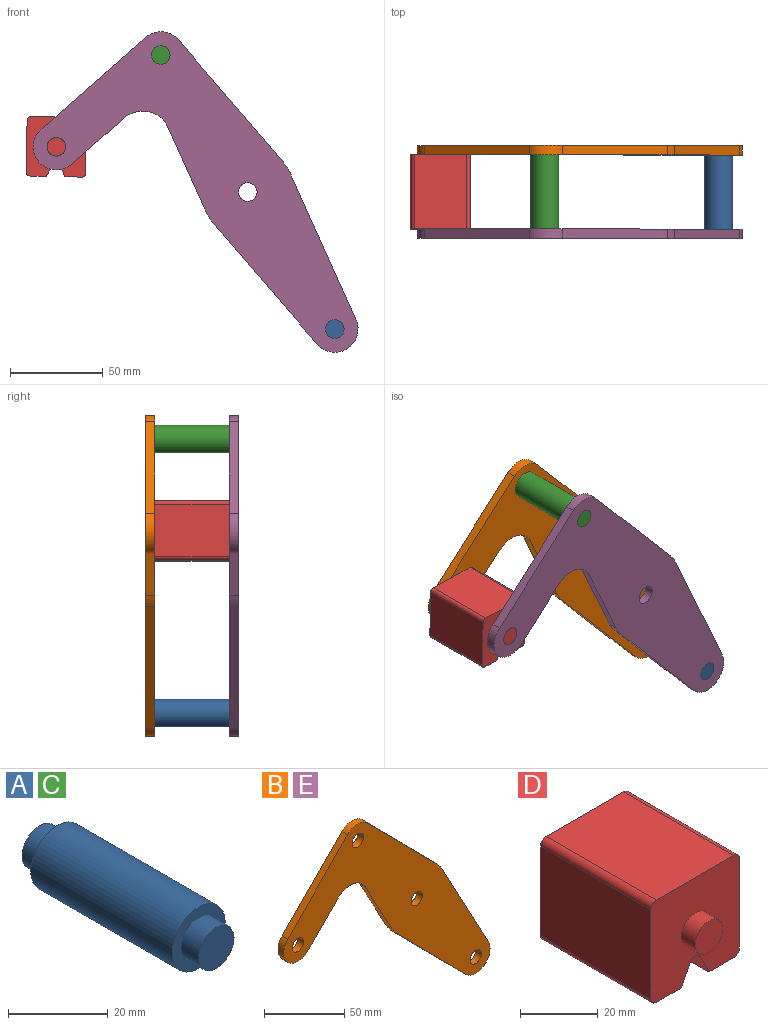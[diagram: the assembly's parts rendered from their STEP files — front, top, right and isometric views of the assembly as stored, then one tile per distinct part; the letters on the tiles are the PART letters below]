
ASSEMBLY  parts=5 mates=3
PART A: 7 faces, bbox 15x50x15 mm
  f0: cylinder r=7.5mm len=40mm, axis (0,-1,0), area 1885mm2, adj f2,f5
  f1: cylinder r=5mm len=10mm, axis (0,1,0), area 157.1mm2, adj f2,f3
  f2: plane 15x15mm, normal (0,-1,0), area 98.2mm2, adj f0,f1
  f3: plane 10x10mm, normal (0,-1,0), area 78.5mm2, adj f1
  f4: cylinder r=5mm len=10mm, axis (0,-1,0), area 157.1mm2, adj f5,f6
  f5: plane 15x15mm, normal (0,1,0), area 98.2mm2, adj f0,f4
  f6: plane 10x10mm, normal (0,1,0), area 78.5mm2, adj f4
PART B: 18 faces, bbox 181.7x5x165.8 mm
  f0: plane 43.49x23.35mm, normal (-0.88,0,-0.47), area 246.8mm2, adj f1,f14,f16,f17
  f1: cylinder r=25mm len=5.75mm, axis (0,1,0), area 35.8mm2, adj f0,f2,f16,f17
  f2: plane 61.6x60.87mm, normal (-0.71,0,-0.7), area 433mm2, adj f1,f3,f16,f17
  f3: cylinder r=12.5mm len=21.39mm, axis (0,1,0), area 178.4mm2, adj f2,f4,f16,f17
  f4: plane 76.3x40.96mm, normal (0.88,0,0.47), area 433mm2, adj f3,f5,f16,f17
  f5: cylinder r=25mm len=5.75mm, axis (0,1,0), area 35.8mm2, adj f4,f6,f16,f17
  f6: plane 61.6x60.87mm, normal (0.71,0,0.7), area 433mm2, adj f5,f7,f16,f17
  f7: cylinder r=12.5mm len=17.78mm, axis (0,1,0), area 98.9mm2, adj f6,f8,f16,f17
  f8: plane 53.35x52.71mm, normal (-0.71,0,0.7), area 375mm2, adj f7,f9,f16,f17
  f9: cylinder r=12.5mm len=21.39mm, axis (0,1,0), area 196.3mm2, adj f8,f10,f16,f17
  f10: plane 26.86x26.54mm, normal (0.71,0,-0.7), area 188.8mm2, adj f9,f14,f16,f17
  f11: cylinder r=5mm len=10mm, axis (0,1,0), area 157.1mm2, adj f16,f17
  f12: cylinder r=5mm len=10mm, axis (0,1,0), area 157.1mm2, adj f16,f17
  f13: cylinder r=5mm len=10mm, axis (0,1,0), area 157.1mm2, adj f16,f17
  f14: cylinder r=15mm len=23.89mm, axis (0,1,0), area 140.2mm2, adj f0,f10,f16,f17
  f15: cylinder r=5mm len=10mm, axis (0,1,0), area 157.1mm2, adj f16,f17
  f16: plane 181.66x165.78mm, normal (0,-1,0), area 8710.1mm2, adj f0,f1,f2,f3,f4,f5,f6,f7
  f17: plane 181.66x165.78mm, normal (0,1,0), area 8710.1mm2, adj f0,f1,f2,f3,f4,f5,f6,f7
PART C: same geometry as A
PART D: 18 faces, bbox 32.1x50x32.1 mm
  f0: plane 40x28.08mm, normal (1,0,0), area 1123.1mm2, adj f4,f10,f13,f14
  f1: plane 40x9.04mm, normal (0,0,-1), area 361.6mm2, adj f2,f4,f10,f14
  f2: plane 40x6.42mm, normal (-0.89,0,-0.45), area 287.2mm2, adj f1,f4,f10,f15
  f3: plane 40x6.42mm, normal (0.89,0,-0.45), area 287.2mm2, adj f4,f5,f10,f15
  f4: plane 32.08x32.08mm, normal (0,-1,0), area 900.6mm2, adj f0,f1,f2,f3,f5,f6,f7,f9
  f5: plane 40x9.04mm, normal (0,0,-1), area 361.6mm2, adj f3,f4,f10,f16
  f6: plane 40x28.08mm, normal (0,0,1), area 1123.1mm2, adj f4,f10,f13,f17
  f7: plane 40x28.08mm, normal (-1,0,0), area 1123.1mm2, adj f4,f10,f16,f17
  f8: plane 10x10mm, normal (0,-1,0), area 78.5mm2, adj f9
  f9: cylinder r=5mm len=10mm, axis (0,1,0), area 157.1mm2, adj f4,f8
  f10: plane 32.08x32.08mm, normal (0,1,0), area 900.6mm2, adj f0,f1,f2,f3,f5,f6,f7,f12
  f11: plane 10x10mm, normal (0,1,0), area 78.5mm2, adj f12
  f12: cylinder r=5mm len=10mm, axis (0,-1,0), area 157.1mm2, adj f10,f11
  f13: cylinder r=2mm len=40mm, axis (0,1,0), area 125.7mm2, adj f0,f4,f6,f10
  f14: cylinder r=2mm len=40mm, axis (0,-1,0), area 125.7mm2, adj f0,f1,f4,f10
  f15: cylinder r=2mm len=40mm, axis (0,1,0), area 177.1mm2, adj f2,f3,f4,f10
  f16: cylinder r=2mm len=40mm, axis (0,1,0), area 125.7mm2, adj f4,f5,f7,f10
  f17: cylinder r=2mm len=40mm, axis (0,-1,0), area 125.7mm2, adj f4,f6,f7,f10
PART E: same geometry as B
PLACE A rot(axis=(0,1,0),4deg) t=(93.78,-20,-147.75)mm
PLACE B rot(axis=(0,1,0),4deg) t=(0,25,0)mm
PLACE C rot(axis=(0,1,0),4deg) t=(0,-20,0)mm
PLACE D rot(axis=(0,1,0),1.2deg) t=(1.07,-20,5.1)mm
PLACE E rot(axis=(0,1,0),4deg) t=(0,-20,0)mm fixed
MATE fastened C.f0 <-> B.f7  axis (0,1,0) through (-46.89,20,73.87)mm
MATE revolute D.f9 <-> E.f9  axis (0,-1,0) through (-103.23,-20,24.37)mm
MATE fastened E.f3 <-> A.f0  axis (0,1,0) through (46.89,-20,-73.87)mm
